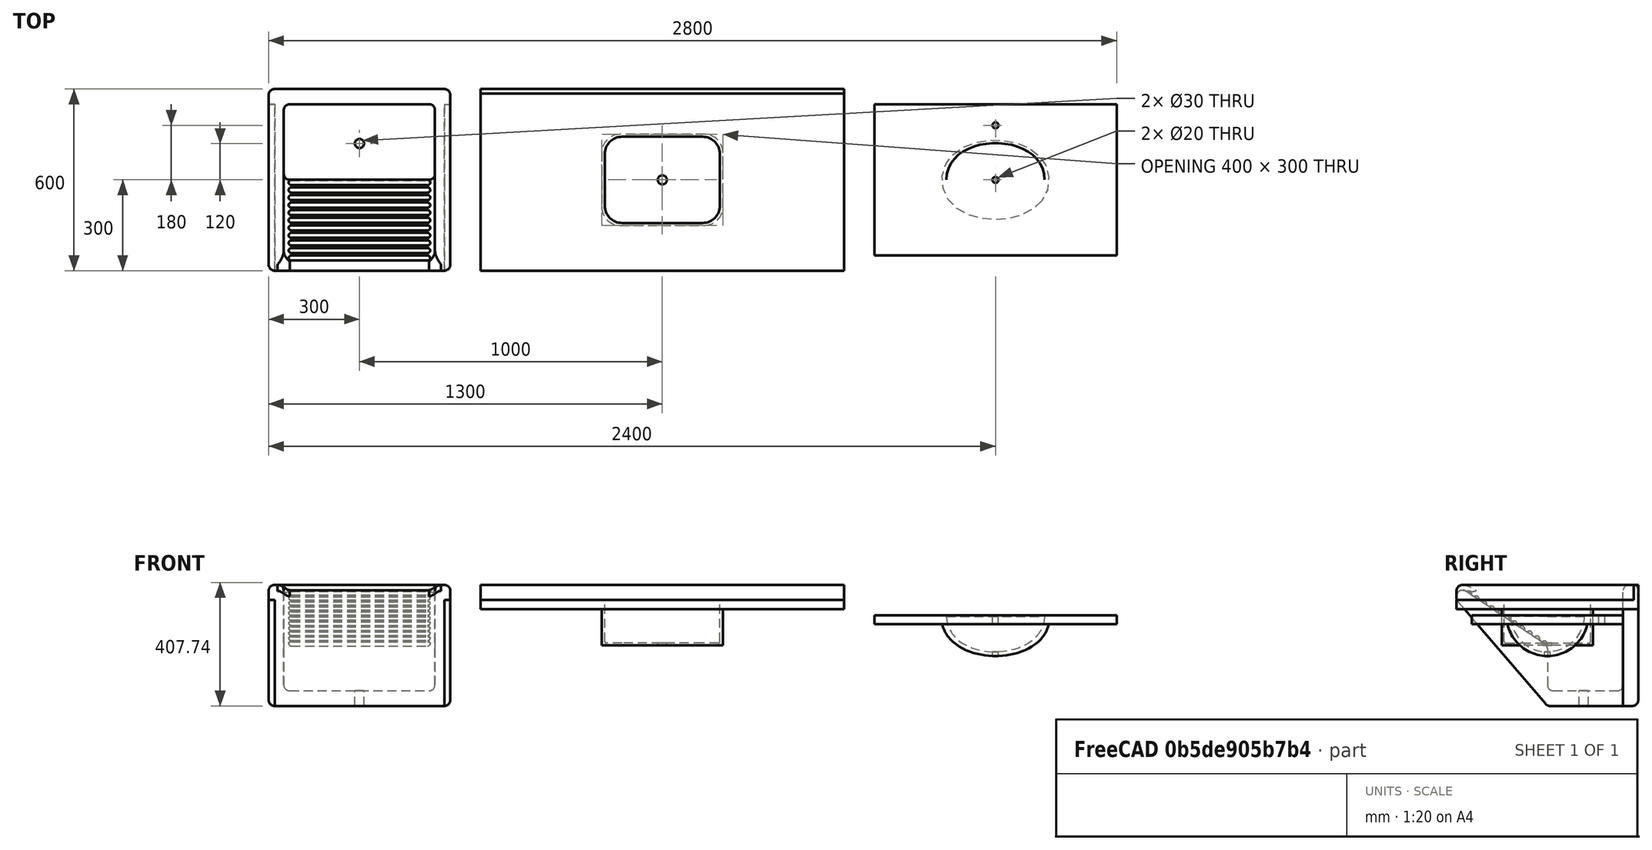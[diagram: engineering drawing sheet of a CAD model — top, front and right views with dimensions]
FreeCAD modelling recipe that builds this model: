
FCSTD DOCUMENT  (FreeCAD 0.16R6706 (Git))
Label: models
License: All rights reserved
LicenseURL: http://en.wikipedia.org/wiki/All_rights_reserved
objects: Part::Cut×9, Part::Cylinder×4, Part::MultiFuse×3, Part::Extrusion×3, Part::FeaturePython×3, Part::Feature×2, Part::Fillet×2, Part::Part2DObjectPython×1, Part::Mirroring×1
note: 28 computed .brp shape members not serialized (recipe doc carries the construction recipe); baked Part::Feature solids carry a one-line shape summary decoded from their .brp

FEATURE [Part::MultiFuse] Fusion001
  Placement = pos=(0,0,800) rot=(0,0,1;0rad)
FEATURE [Part::Cylinder] Cylinder
  Angle = 360
  Height = 1000
  Placement = pos=(0,300,500) rot=(0,0,1;0rad)
  Radius = 15
FEATURE [Part::Cut] Cut  label="sink"
  Base = -> Fusion001
  Placement = pos=(1000,-300,0) rot=(0,0,1;0rad)
  Tool = -> Cylinder
FEATURE [Part::Feature] Face
  shape: bbox 600 x 2e-07 x 400 mm, 1 faces, 0 solids (baked)
FEATURE [Part::Feature] Face001
  shape: bbox 550 x 2e-07 x 350 mm, 1 faces, 0 solids (baked)
FEATURE [Part::Extrusion] Extrusion
  Base = -> Face
  Dir = (0,-600,0)
  Solid = true
FEATURE [Part::Extrusion] Extrusion001
  Base = -> Face001
  Dir = (0,-499.351,0)
  Placement = pos=(0,-50,0) rot=(0,0,1;0rad)
  Solid = true
FEATURE [Part::Cut] Cut001
  Base = -> Extrusion
  Tool = -> Extrusion001
FEATURE [Part::Fillet] Fillet
  Base = -> Cut001
  Edges = 31 edges r=20: [Edge1,Edge2,Edge3,Edge4,Edge5,Edge6,Edge7,Edge8,Edge9,Edge10,Edge11,Edge12,Edge13,Edge14,Edge15,Edge16,Edge17,Edge18,Edge19,Edge20,Edge21,Edge22,Edge23,Edge24,Edge25,Edge26,Edge27,Edge28,Edge29,Edge30,Edge31]
FEATURE [Part::FeaturePython] Clone  label="Clone of Fusion001"  # WARN: FeaturePython — macro-defined, semantics opaque (R4)
  Placement = pos=(0,-280,0) rot=(0,0,1;0rad)
  Scale = (1,0.9,1)
FEATURE [Part::FeaturePython] Array  # Draft array (typed FeaturePython)
  Angle = 360
  ArrayType = 0
  Axis = (0,0,1)
  Base = -> Clone
  Center = (0,0,0)
  Fuse = false
  IntervalAxis = (0,0,0)
  IntervalX = (30,0,0)
  IntervalY = (0,1,0)
  IntervalZ = (0,0,0)
  NumberPolar = 1
  NumberX = 11
  NumberY = 1
  NumberZ = 1
  Placement = pos=(-260,0,170) rot=(0,1,0;0.584685rad)
FEATURE [Part::MultiFuse] Fusion
  Placement = pos=(0,300,800) rot=(0,0,1;0rad)
  Shapes = -> [Fillet,Array]
FEATURE [Part::Part2DObjectPython] Rectangle  # Draft 2D object (typed FeaturePython)
  ChamferSize = 0
  Columns = 1
  FilletRadius = 0
  Height = 100
  Length = -800
  MakeFace = true
  Placement = pos=(400,-380,0) rot=(0,0,1;0rad)
  Rows = 1
FEATURE [Part::Extrusion] Extrusion002
  Base = -> Rectangle
  Dir = (0,0,900)
  Placement = pos=(-150,0,50) rot=(0,0,1;0rad)
  Solid = true
FEATURE [Part::Mirroring] mirror  label="Mirror of Clone of Extrusion002"
  Base = (-1000,0,0)
  Normal = (0,-1,0)
FEATURE [Part::Cut] Cut002
  Base = -> Fusion
  Tool = -> Extrusion002
FEATURE [Part::Cut] Cut003
  Base = -> Cut002
  Tool = -> mirror
FEATURE [Part::Cylinder] Cylinder001
  Angle = 360
  Height = 1000
  Placement = pos=(120,0,0) rot=(0,0,1;0rad)
  Radius = 15
FEATURE [Part::Cut] Cut004  label="tanque"
  Base = -> Cut003
  Placement = pos=(0,0,0) rot=(0,0,1;1.5708rad)
  Tool = -> Cylinder001
FEATURE [Part::Cut] Cut005
  Placement = pos=(0,0,300) rot=(0,0,1;0rad)
FEATURE [Part::FeaturePython] Clone003  label="fundo"  # WARN: FeaturePython — macro-defined, semantics opaque (R4)
  Placement = pos=(0,0,550) rot=(0,0,1;0rad)
  Scale = (0.9,0.9,0.9)
FEATURE [Part::Cut] Cut006
  Tool = -> Clone003
FEATURE [Part::Fillet] Fillet001
  Base = -> Cut006
  Edges = 2 edges r=5: [Edge6,Edge8]
  Placement = pos=(0,0,300) rot=(0,0,1;0rad)
FEATURE [Part::Cylinder] Cylinder002
  Angle = 360
  Height = 1000
  Radius = 10
FEATURE [Part::Cut] Cut007
  Base = -> Fillet001
  Tool = -> Cylinder002
FEATURE [Part::Cylinder] Cylinder003
  Angle = 360
  Height = 1000
  Placement = pos=(0,180,0) rot=(0,0,1;0rad)
  Radius = 10
FEATURE [Part::Cut] Cut008
  Base = -> Cut005
  Tool = -> Cylinder003
FEATURE [Part::MultiFuse] Fusion002  label="lavat"
  Placement = pos=(2100,0,100) rot=(0,0,1;0rad)
  Shapes = -> [Cut008,Cut007]
